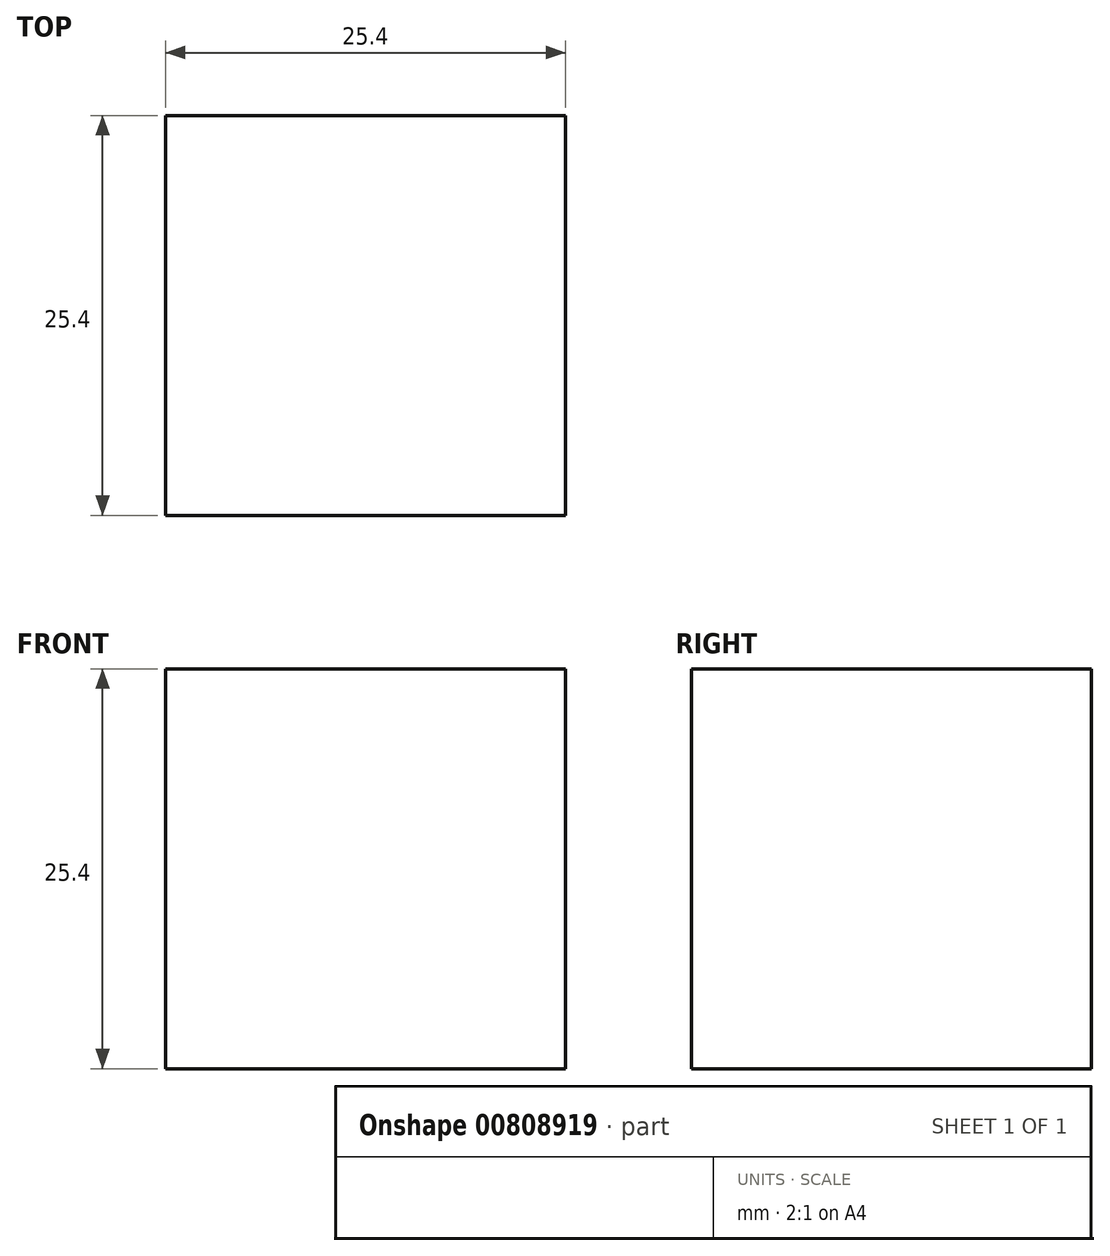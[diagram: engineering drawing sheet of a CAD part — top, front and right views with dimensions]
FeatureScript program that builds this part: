
annotation { "Feature Type Name" : "Feature", "Feature Type Description" : "" }
export const myFeature = defineFeature(function(context is Context, id is Id, definition is map)
    precondition{}
    {
        {
            var Q0;
            Q0=qCreatedBy(makeId("Top.planeOp"),FACE);
            var sketch = newSketch(context, id + "F0", { "sketchPlane" : qUnion([Q0])});
            skLineSegment(sketch, "E0.bottom", {"start": v(0, 0) * mm, "end": v(25.4, 0) * mm});
            skLineSegment(sketch, "E0.top", {"start": v(0, -25.4) * mm, "end": v(25.4, -25.4) * mm});
            skLineSegment(sketch, "E0.left", {"start": v(0, 0) * mm, "end": v(0, -25.4) * mm});
            skLineSegment(sketch, "E0.right", {"start": v(25.4, 0) * mm, "end": v(25.4, -25.4) * mm});
            skSolve(sketch);
        }
        {
            var Q0;
            Q0=makeQuery(id+"F0.imprint","IMPRINT",FACE,{"disambiguationData":[TD([[makeQuery(id+"F0.imprint","IMPRINT",EDGE,{"derivedFrom":sQuery(id+"F0.wireOp",EDGE,"E0.bottom")}),-1.0]])]});
            extrude(context, id + "F1", {"entities" : qUnion([Q0]), "depth" : 25.4 * mm, "offsetDistance" : 25.4 * mm});
        }
    });
